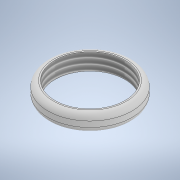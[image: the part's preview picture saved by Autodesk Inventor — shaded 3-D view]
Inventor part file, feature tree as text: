
AUTODESK INVENTOR PART (.ipt)
format: ipt  version: 2021 (Build 250183000, 183)  size: 144,384 bytes
history: native  units: mm
features: extrude x2, sketch x2, fillet x1, other x1
ambient origin geometry x8: Origin, YZ Plane, XZ Plane, XY Plane, X Axis, Y Axis, Z Axis, Center Point
bodies: Body1 (feature_tree)
feature tree (6):
  extrude  "Extrusion1"  Depth=30.0mm
  fillet  "Congé1"  Radius=6.0mm
  extrude  "Extrusion2"  Depth=2.0mm
  other  "Filetage2"
  sketch  "Esquisse1"
  sketch  "Esquisse2"
